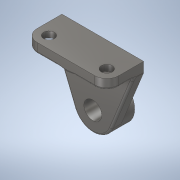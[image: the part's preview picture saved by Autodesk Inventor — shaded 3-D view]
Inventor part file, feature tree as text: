
AUTODESK INVENTOR PART (.ipt)
format: ipt  version: 2020 (Build 240168000, 168)  size: 385,536 bytes
history: native  units: mm
features: extrude x5, sketch x4, fillet x2, plane x1, rib x1
ambient origin geometry x8: Origin, YZ Plane, XZ Plane, XY Plane, X Axis, Y Axis, Z Axis, Center Point
bodies: Solid1 (feature_tree)
feature tree (13):
  extrude  "Extrusion1"  Depth=41.0mm
  sketch  "Sketch2"  dims[d2=18.0mm d3=22.0mm d4=0.0mm]
  extrude  "Extrusion2"  Depth=22.0mm TaperAngle=0.0deg
  extrude  "Extrusion3"  Depth=41.0mm
  plane  "Work Plane1"
  rib  "Rib1"
  sketch  "Sketch6"  dims[d7=10.0mm d8=10.0mm d9=0.0mm d10=27.0mm d11=0.0mm d12=-41.0mm d17=1.0mm d18=10.0mm d19=0.0mm d20=0.0mm d21=1.0mm d22=1.0mm d23=11.0mm d24=22.0mm d25=22.0mm d26=11.0mm d27=12.0mm d28=12.0mm d29=12.0mm d30=12.0mm d31=27.0mm d32=0.0mm d33=4.0mm d34=0.0mm d35=12.0mm d37=2.0mm]
  extrude  "Extrusion4"  Depth=10.0mm TaperAngle=0.0deg
  extrude  "Extrusion5"  Depth=27.0mm TaperAngle=0.0deg
  fillet  "Fillet1"  [1 undecoded]
  fillet  "Fillet3"  Radius=1.0mm
  sketch  "Sketch1"  dims[d0=40.0mm d1=41.0mm]
  sketch  "Sketch5"  dims[d5=82.0mm d6=41.0mm]
note: 1 required parameter value undecoded (feature->parameter linkage not recoverable at this tier; creation-order binding heuristic only, values carry confidence <= 0.55)
